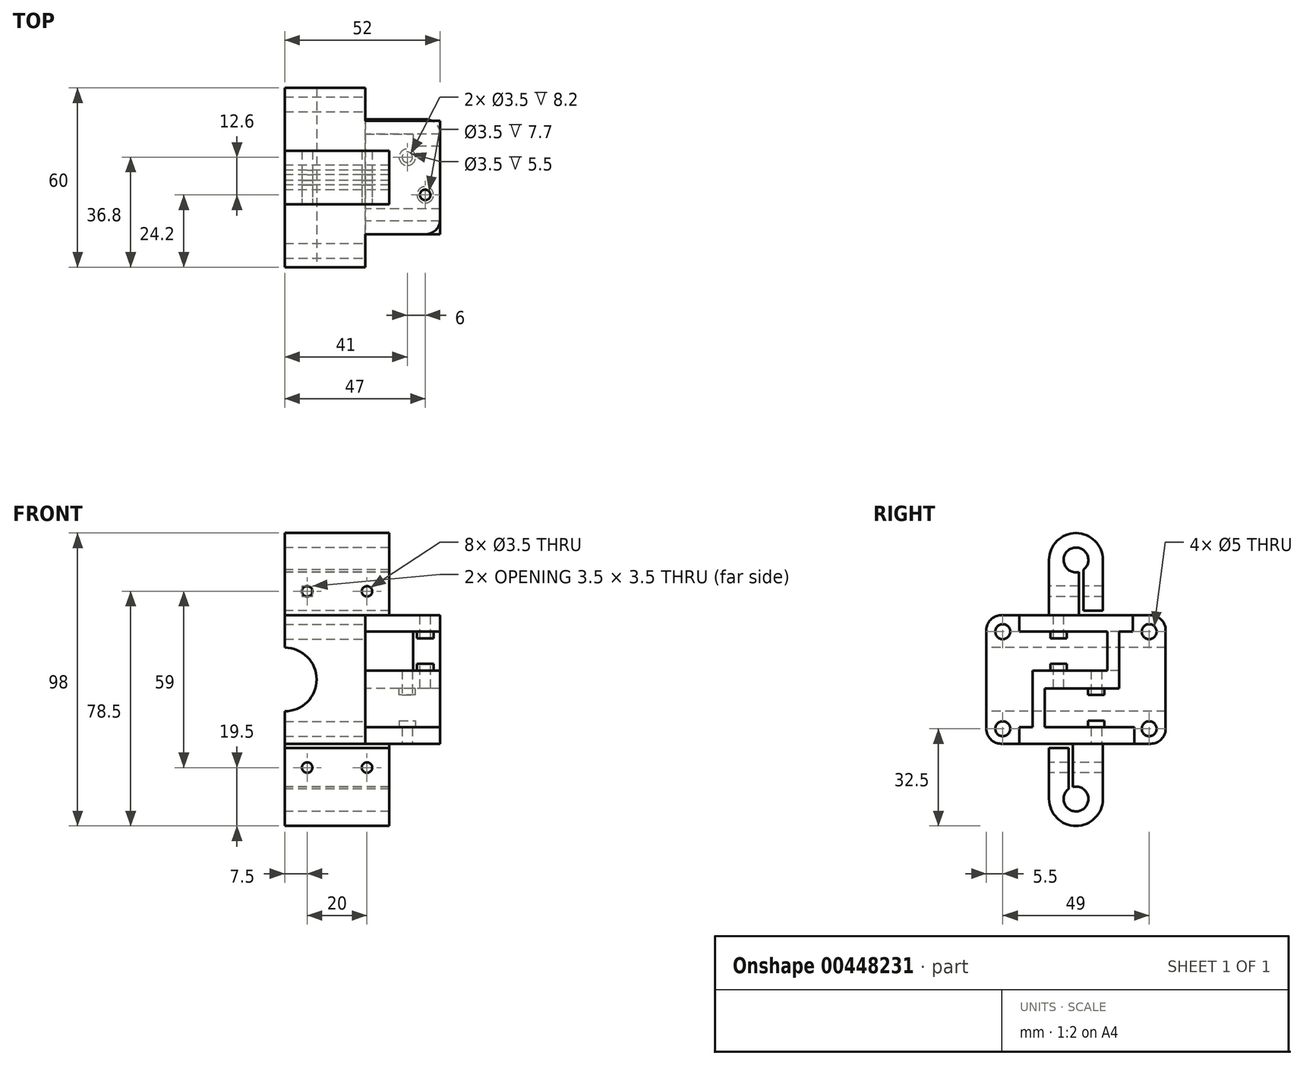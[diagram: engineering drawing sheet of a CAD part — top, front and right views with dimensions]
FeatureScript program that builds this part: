
annotation { "Feature Type Name" : "Feature", "Feature Type Description" : "" }
export const myFeature = defineFeature(function(context is Context, id is Id, definition is map)
    precondition{}
    {
        {
            var Q0;
            Q0=qCreatedBy(makeId("Front.planeOp"),FACE);
            var sketch = newSketch(context, id + "F0", { "sketchPlane" : qUnion([Q0])});
            skLineSegment(sketch, "E0.bottom", {"start": v(27, 21.5) * mm, "end": v(0, 21.5) * mm});
            skLineSegment(sketch, "E0.top", {"start": v(27, -21.5) * mm, "end": v(0, -21.5) * mm});
            skLineSegment(sketch, "E0.left", {"start": v(27, 21.5) * mm, "end": v(27, -21.5) * mm});
            skLineSegment(sketch, "E0.right", {"start": v(0, 21.5) * mm, "end": v(0, -21.5) * mm});
            skPoint(sketch, "E0.middle", {"position": v(0, 0) * mm});
            skSolve(sketch);
        }
        {
            var Q0;
            Q0=makeQuery(id+"F0.imprint","IMPRINT",FACE,{"disambiguationData":[TD([[makeQuery(id+"F0.imprint","IMPRINT",EDGE,{"derivedFrom":sQuery(id+"F0.wireOp",EDGE,"E0.bottom")}),1.0]])]});
            extrude(context, id + "F1", {"entities" : qUnion([Q0]), "endBound" : BoundingType.SYMMETRIC, "depth" : 60 * mm});
        }
        {
            var Q0;
            Q0=makeQuery(id+"F1.opExtrude","CAP_FACE",FACE,{"disambiguationData":[OSD([sQuery(id+"F0.wireOp",EDGE,"E0.bottom"),sQuery(id+"F0.wireOp",EDGE,"E0.top"),sQuery(id+"F0.wireOp",EDGE,"E0.left"),sQuery(id+"F0.wireOp",EDGE,"E0.right")])],"isStart":false});
            var sketch = newSketch(context, id + "F2", { "sketchPlane" : qUnion([Q0])});
            skCircle(sketch, "E1", {"center": v(0, 0) * mm, "radius": 10.65 * mm});
            skSolve(sketch);
        }
        {
            var Q0;
            {var subQ0=sQuery(id+"F2.wireOp",EDGE,"E1");var subQ1=makeQuery(id+"F1.opExtrude","CAP_EDGE",EDGE,{"disambiguationData":[OSD([sQuery(id+"F0.wireOp",EDGE,"E0.right")])],"isStart":false});var subQ2=makeQuery(id+"F2.imprint","INTERSECT",VERTEX,{"disambiguationData":[OD(0.0)],"derivedFrom":[subQ1,subQ0]});Q0=makeQuery(id+"F2.imprint","IMPRINT",FACE,{"disambiguationData":[TD([[makeQuery(id+"F2.imprint","IMPRINT",EDGE,{"disambiguationData":[TD([[subQ2,1.0]])],"derivedFrom":subQ0}),1.0]])]});}
            var Q1;
            {var subQ0=sQuery(id+"F2.wireOp",EDGE,"E1");var subQ1=makeQuery(id+"F1.opExtrude","CAP_EDGE",EDGE,{"disambiguationData":[OSD([sQuery(id+"F0.wireOp",EDGE,"E0.right")])],"isStart":false});var subQ2=makeQuery(id+"F2.imprint","INTERSECT",VERTEX,{"disambiguationData":[OD(0.0)],"derivedFrom":[subQ1,subQ0]});Q1=makeQuery(id+"F2.imprint","IMPRINT",FACE,{"disambiguationData":[TD([[makeQuery(id+"F2.imprint","IMPRINT",EDGE,{"disambiguationData":[TD([[subQ2,-1.0]])],"derivedFrom":subQ0}),1.0]])]});}
            var Q2;
            Q2=makeQuery(id+"F1.opExtrude","CAP_FACE",FACE,{"disambiguationData":[OSD([sQuery(id+"F0.wireOp",EDGE,"E0.bottom"),sQuery(id+"F0.wireOp",EDGE,"E0.top"),sQuery(id+"F0.wireOp",EDGE,"E0.left"),sQuery(id+"F0.wireOp",EDGE,"E0.right")])],"isStart":true});
            extrude(context, id + "F3", {"entities" : qUnion([Q0, Q1]), "operationType" : NewBodyOperationType.REMOVE, "endBound" : BoundingType.THROUGH_ALL, "oppositeDirection" : true, "endBoundEntityFace" : qUnion([Q2]), "depth" : 67.7 * mm});
        }
        {
            var Q0;
            Q0=makeQuery(id+"F1.opExtrude","SWEPT_FACE",FACE,{"disambiguationData":[OSD([sQuery(id+"F0.wireOp",EDGE,"E0.left")])]});
            var sketch = newSketch(context, id + "F4", { "sketchPlane" : qUnion([Q0])});
            skPoint(sketch, "E2", {"position": v(-24.5, 16) * mm});
            skPoint(sketch, "E3.1.0.0", {"position": v(24.5, 16) * mm});
            skLineSegment(sketch, "E3.direction1", {"start": v(-24.5, 16) * mm, "end": v(24.5, 16) * mm, "construction": true});
            skPoint(sketch, "E4.1.0.0", {"position": v(-24.5, -16.5) * mm});
            skPoint(sketch, "E4.1.0.1", {"position": v(24.5, -16.5) * mm});
            skLineSegment(sketch, "E4.direction1", {"start": v(-24.5, 16) * mm, "end": v(-24.5, -16.5) * mm, "construction": true});
            skSolve(sketch);
        }
        {
            var Q0;
            Q0=sQuery(id+"F4.wireOp",VERTEX,"E2");
            var Q1;
            Q1=sQuery(id+"F4.wireOp",VERTEX,"E3.1.0.0");
            var Q2;
            Q2=sQuery(id+"F4.wireOp",VERTEX,"E4.1.0.1");
            var Q3;
            Q3=sQuery(id+"F4.wireOp",VERTEX,"E4.1.0.0");
            var Q4;
            Q4=makeQuery(id+"F1.opExtrude","SWEPT_BODY",BODY,{"disambiguationData":[OSD([sQuery(id+"F0.wireOp",EDGE,"E0.bottom"),sQuery(id+"F0.wireOp",EDGE,"E0.top"),sQuery(id+"F0.wireOp",EDGE,"E0.left"),sQuery(id+"F0.wireOp",EDGE,"E0.right")])]});
            hole(context, id + "F5", {"style" : HoleStyle.SIMPLE, "endStyle" : HoleEndStyle.THROUGH, "holeDiameter" : 5 * mm, "isTappedThrough" : true, "tappedDepth" : 12 * mm, "tapClearance" : 3, "locations" : qUnion([Q0, Q1, Q2, Q3]), "scope" : qUnion([Q4])});
        }
        {
            var Q0;
            {var subQ0=sQuery(id+"F0.wireOp",EDGE,"E0.right");var subQ2=sQuery(id+"F0.wireOp",EDGE,"E0.top");Q0=makeQuery(id+"F3.boolean.opBoolean","SPLIT",FACE,{"disambiguationData":[TD([makeQuery(id+"F1.opExtrude","SWEPT_FACE",FACE,{"disambiguationData":[OSD([subQ2])]})])],"derivedFrom":makeQuery(id+"F1.opExtrude","SWEPT_FACE",FACE,{"disambiguationData":[OSD([subQ0])]})});}
            var sketch = newSketch(context, id + "F6", { "sketchPlane" : qUnion([Q0])});
            skLineSegment(sketch, "E5.bottom", {"start": v(9, 21.5) * mm, "end": v(-9, 21.5) * mm});
            skLineSegment(sketch, "E5.top", {"start": v(9, 40) * mm, "end": v(-9, 40) * mm});
            skLineSegment(sketch, "E5.left", {"start": v(9, 21.5) * mm, "end": v(9, 40) * mm});
            skLineSegment(sketch, "E5.right", {"start": v(-9, 21.5) * mm, "end": v(-9, 40) * mm});
            skLineSegment(sketch, "E6.bottom", {"start": v(9, -21.5) * mm, "end": v(-9, -21.5) * mm});
            skLineSegment(sketch, "E6.top", {"start": v(9, -40) * mm, "end": v(-9, -40) * mm});
            skLineSegment(sketch, "E6.left", {"start": v(9, -21.5) * mm, "end": v(9, -40) * mm});
            skLineSegment(sketch, "E6.right", {"start": v(-9, -21.5) * mm, "end": v(-9, -40) * mm});
            skArc(sketch, "E7", {"start": v(9, 40) * mm, "mid": v(0, 49) * mm, "end": v(-9, 40) * mm});
            skArc(sketch, "E8", {"start": v(-9, -40) * mm, "mid": v(0, -49) * mm, "end": v(9, -40) * mm});
            skLineSegment(sketch, "E9", {"start": v(0, 21.5) * mm, "end": v(0, -21.5) * mm, "construction": true});
            skPoint(sketch, "E9.startSnap0", {"position": v(0, 21.5) * mm});
            skSolve(sketch);
        }
        {
            var Q0;
            Q0=makeQuery(id+"F6.imprint","IMPRINT",FACE,{"disambiguationData":[TD([[makeQuery(id+"F6.imprint","IMPRINT",EDGE,{"derivedFrom":sQuery(id+"F6.wireOp",EDGE,"E5.bottom")}),-1.0]])]});
            var Q1;
            Q1=makeQuery(id+"F6.imprint","IMPRINT",FACE,{"disambiguationData":[TD([[makeQuery(id+"F6.imprint","IMPRINT",EDGE,{"derivedFrom":sQuery(id+"F6.wireOp",EDGE,"E5.top")}),-1.0]])]});
            var Q2;
            Q2=makeQuery(id+"F6.imprint","IMPRINT",FACE,{"disambiguationData":[TD([[makeQuery(id+"F6.imprint","IMPRINT",EDGE,{"derivedFrom":sQuery(id+"F6.wireOp",EDGE,"E6.bottom")}),1.0]])]});
            var Q3;
            Q3=makeQuery(id+"F6.imprint","IMPRINT",FACE,{"disambiguationData":[TD([[makeQuery(id+"F6.imprint","IMPRINT",EDGE,{"derivedFrom":sQuery(id+"F6.wireOp",EDGE,"E6.top")}),1.0]])]});
            extrude(context, id + "F7", {"entities" : qUnion([Q0, Q1, Q2, Q3]), "operationType" : NewBodyOperationType.ADD, "oppositeDirection" : true, "depth" : 35 * mm});
        }
        {
            var Q0;
            Q0=sQuery(id+"F6.wireOp",VERTEX,"E8.center");
            var Q1;
            Q1=sQuery(id+"F6.wireOp",VERTEX,"E7.center");
            var Q2;
            Q2=makeQuery(id+"F1.opExtrude","SWEPT_BODY",BODY,{"disambiguationData":[OSD([sQuery(id+"F0.wireOp",EDGE,"E0.bottom"),sQuery(id+"F0.wireOp",EDGE,"E0.top"),sQuery(id+"F0.wireOp",EDGE,"E0.left"),sQuery(id+"F0.wireOp",EDGE,"E0.right")])]});
            hole(context, id + "F8", {"style" : HoleStyle.SIMPLE, "endStyle" : HoleEndStyle.THROUGH, "holeDiameter" : 8.3 * mm, "isTappedThrough" : true, "tappedDepth" : 12 * mm, "tapClearance" : 3, "locations" : qUnion([Q0, Q1]), "scope" : qUnion([Q2])});
        }
        {
            var Q0;
            Q0=makeQuery(id+"F1.opExtrude","SWEPT_FACE",FACE,{"disambiguationData":[OSD([sQuery(id+"F0.wireOp",EDGE,"E0.left")])]});
            var sketch = newSketch(context, id + "F9", { "sketchPlane" : qUnion([Q0])});
            skLineSegment(sketch, "E10", {"start": v(-19, 21.5) * mm, "end": v(-19, 16) * mm});
            skLineSegment(sketch, "E11", {"start": v(-19, 16) * mm, "end": v(10.5, 16) * mm});
            skLineSegment(sketch, "E12", {"start": v(10.5, 16) * mm, "end": v(10.5, 3) * mm});
            skLineSegment(sketch, "E13", {"start": v(-10.5, -3) * mm, "end": v(14.5, -3) * mm});
            skLineSegment(sketch, "E14", {"start": v(14.5, -3) * mm, "end": v(14.5, 16) * mm});
            skLineSegment(sketch, "E15", {"start": v(14.5, 16) * mm, "end": v(19, 16) * mm});
            skLineSegment(sketch, "E16", {"start": v(19, 16) * mm, "end": v(19, 21.5) * mm});
            skLineSegment(sketch, "E17", {"start": v(19, 21.5) * mm, "end": v(-19, 21.5) * mm});
            skLineSegment(sketch, "E18", {"start": v(10.5, 3) * mm, "end": v(-14.5, 3) * mm});
            skLineSegment(sketch, "E19", {"start": v(-12, -21.5) * mm, "end": v(19.5, -21.5) * mm});
            skLineSegment(sketch, "E20", {"start": v(19.5, -21.5) * mm, "end": v(19.5, -16) * mm});
            skLineSegment(sketch, "E21", {"start": v(19.5, -16) * mm, "end": v(-14.68, -16) * mm});
            skLineSegment(sketch, "E22", {"start": v(-8.55, -16) * mm, "end": v(-19, -16) * mm});
            skLineSegment(sketch, "E23", {"start": v(-19, -16) * mm, "end": v(-19, -21.5) * mm});
            skLineSegment(sketch, "E24", {"start": v(-19, -21.5) * mm, "end": v(19.5, -21.5) * mm});
            skLineSegment(sketch, "E25", {"start": v(-10.5, -16) * mm, "end": v(-10.5, -3) * mm});
            skLineSegment(sketch, "E26", {"start": v(-14.5, 3) * mm, "end": v(-14.5, -16) * mm});
            skSolve(sketch);
        }
        {
            var Q0;
            {var subQ12=sQuery(id+"F9.wireOp",EDGE,"E10");Q0=makeQuery(id+"F9.imprint","IMPRINT",FACE,{"disambiguationData":[TD([[makeQuery(id+"F9.imprint","IMPRINT",EDGE,{"derivedFrom":subQ12}),1.0]])]});}
            var Q1;
            {var subQ5=sQuery(id+"F9.wireOp",EDGE,"E20");Q1=makeQuery(id+"F9.imprint","IMPRINT",FACE,{"disambiguationData":[TD([[makeQuery(id+"F9.imprint","IMPRINT",EDGE,{"derivedFrom":subQ5}),1.0]])]});}
            extrude(context, id + "F10", {"entities" : qUnion([Q0, Q1]), "operationType" : NewBodyOperationType.ADD, "depth" : 25 * mm});
        }
        {
            var Q0;
            Q0=makeQuery(id+"F10.opExtrude","SWEPT_FACE",FACE,{"disambiguationData":[OSD([sQuery(id+"F9.wireOp",EDGE,"E12")])]});
            var sketch = newSketch(context, id + "F11", { "sketchPlane" : qUnion([Q0])});
            skLineSegment(sketch, "E27.bottom", {"start": v(27, 16) * mm, "end": v(43, 16) * mm});
            skLineSegment(sketch, "E27.top", {"start": v(27, 3) * mm, "end": v(43, 3) * mm});
            skLineSegment(sketch, "E27.left", {"start": v(27, 16) * mm, "end": v(27, 3) * mm});
            skLineSegment(sketch, "E27.right", {"start": v(43, 16) * mm, "end": v(43, 3) * mm});
            skSolve(sketch);
        }
        {
            var Q0;
            Q0=makeQuery(id+"F11.imprint","IMPRINT",FACE,{"disambiguationData":[TD([[makeQuery(id+"F11.imprint","IMPRINT",EDGE,{"derivedFrom":sQuery(id+"F11.wireOp",EDGE,"E27.bottom")}),1.0]])]});
            extrude(context, id + "F12", {"entities" : qUnion([Q0]), "operationType" : NewBodyOperationType.REMOVE, "endBound" : BoundingType.UP_TO_NEXT, "oppositeDirection" : true, "depth" : 25 * mm});
        }
        {
            var Q0;
            {var subQ6=sQuery(id+"F6.wireOp",EDGE,"E5.right");var subQ7=sQuery(id+"F6.wireOp",EDGE,"E5.left");var subQ10=sQuery(id+"F0.wireOp",EDGE,"E0.bottom");var subQ11=makeQuery(id+"F1.opExtrude","SWEPT_FACE",FACE,{"disambiguationData":[OSD([subQ10])]});Q0=makeQuery(id+"F10.boolean.opBoolean","MERGE",FACE,{"derivedFrom":[makeQuery(id+"F7.boolean.opBoolean","SPLIT",FACE,{"disambiguationData":[TD([makeQuery(id+"F7.opExtrude","SWEPT_FACE",FACE,{"disambiguationData":[OSD([subQ6])]})])],"derivedFrom":subQ11}),makeQuery(id+"F7.boolean.opBoolean","SPLIT",FACE,{"disambiguationData":[TD([makeQuery(id+"F7.opExtrude","SWEPT_FACE",FACE,{"disambiguationData":[OSD([subQ7])]})])],"derivedFrom":subQ11}),makeQuery(id+"F10.opExtrude","SWEPT_FACE",FACE,{"disambiguationData":[OSD([sQuery(id+"F9.wireOp",EDGE,"E17")])]})]});}
            var sketch = newSketch(context, id + "F13", { "sketchPlane" : qUnion([Q0])});
            skPoint(sketch, "E28", {"position": v(47, -5.8) * mm});
            skSolve(sketch);
        }
        {
            var Q0;
            Q0=sQuery(id+"F13.wireOp",VERTEX,"E28");
            var Q1;
            Q1=makeQuery(id+"F1.opExtrude","SWEPT_BODY",BODY,{"disambiguationData":[OSD([sQuery(id+"F0.wireOp",EDGE,"E0.bottom"),sQuery(id+"F0.wireOp",EDGE,"E0.top"),sQuery(id+"F0.wireOp",EDGE,"E0.left"),sQuery(id+"F0.wireOp",EDGE,"E0.right")])]});
            hole(context, id + "F14", {"style" : HoleStyle.SIMPLE, "endStyle" : HoleEndStyle.BLIND, "holeDiameter" : 3.5 * mm, "holeDepth" : 26 * mm, "isTappedThrough" : true, "tappedDepth" : 12 * mm, "tapClearance" : 3, "locations" : qUnion([Q0]), "scope" : qUnion([Q1])});
        }
        {
            var Q0;
            {var subQ6=sQuery(id+"F0.wireOp",EDGE,"E0.top");var subQ8=sQuery(id+"F6.wireOp",EDGE,"E6.right");var subQ9=sQuery(id+"F6.wireOp",EDGE,"E6.left");var subQ11=makeQuery(id+"F1.opExtrude","SWEPT_FACE",FACE,{"disambiguationData":[OSD([subQ6])]});Q0=makeQuery(id+"F10.boolean.opBoolean","MERGE",FACE,{"derivedFrom":[makeQuery(id+"F7.boolean.opBoolean","SPLIT",FACE,{"disambiguationData":[TD([makeQuery(id+"F7.opExtrude","SWEPT_FACE",FACE,{"disambiguationData":[OSD([subQ8])]})])],"derivedFrom":subQ11}),makeQuery(id+"F7.boolean.opBoolean","SPLIT",FACE,{"disambiguationData":[TD([makeQuery(id+"F7.opExtrude","SWEPT_FACE",FACE,{"disambiguationData":[OSD([subQ9])]})])],"derivedFrom":subQ11}),makeQuery(id+"F10.opExtrude","SWEPT_FACE",FACE,{"disambiguationData":[OSD([sQuery(id+"F9.wireOp",EDGE,"E24")])]})]});}
            var sketch = newSketch(context, id + "F15", { "sketchPlane" : qUnion([Q0])});
            skPoint(sketch, "E29", {"position": v(41, -6.8) * mm});
            skSolve(sketch);
        }
        {
            var Q0;
            Q0=sQuery(id+"F15.wireOp",VERTEX,"E29");
            var Q1;
            Q1=makeQuery(id+"F1.opExtrude","SWEPT_BODY",BODY,{"disambiguationData":[OSD([sQuery(id+"F0.wireOp",EDGE,"E0.bottom"),sQuery(id+"F0.wireOp",EDGE,"E0.top"),sQuery(id+"F0.wireOp",EDGE,"E0.left"),sQuery(id+"F0.wireOp",EDGE,"E0.right")])]});
            hole(context, id + "F16", {"style" : HoleStyle.SIMPLE, "endStyle" : HoleEndStyle.BLIND, "holeDiameter" : 3.5 * mm, "holeDepth" : 26 * mm, "isTappedThrough" : true, "tappedDepth" : 12 * mm, "tapClearance" : 3, "locations" : qUnion([Q0]), "scope" : qUnion([Q1])});
        }
        {
            var Q0;
            Q0=makeQuery(id+"F10.opExtrude","SWEPT_FACE",FACE,{"disambiguationData":[OSD([sQuery(id+"F9.wireOp",EDGE,"E13")])]});
            var sketch = newSketch(context, id + "F17", { "sketchPlane" : qUnion([Q0])});
            skCircle(sketch, "E30.0", {"center": v(41, -6.8) * mm, "radius": 2.75 * mm});
            skSolve(sketch);
        }
        {
            var Q0;
            Q0=makeQuery(id+"F17.imprint","IMPRINT",FACE,{"disambiguationData":[TD([[makeQuery(id+"F17.imprint","IMPRINT",EDGE,{"derivedFrom":sQuery(id+"F17.wireOp",EDGE,"E30.0")}),1.0]])]});
            extrude(context, id + "F18", {"entities" : qUnion([Q0]), "operationType" : NewBodyOperationType.ADD, "depth" : 2.2 * mm});
        }
        {
            var Q0;
            Q0=makeQuery(id+"F10.opExtrude","SWEPT_FACE",FACE,{"disambiguationData":[OSD([sQuery(id+"F9.wireOp",EDGE,"E21"),sQuery(id+"F9.wireOp",EDGE,"E22")])]});
            var sketch = newSketch(context, id + "F19", { "sketchPlane" : qUnion([Q0])});
            skCircle(sketch, "E31.0", {"center": v(41, 6.8) * mm, "radius": 2.75 * mm});
            skSolve(sketch);
        }
        {
            var Q0;
            Q0=makeQuery(id+"F19.imprint","IMPRINT",FACE,{"disambiguationData":[TD([[makeQuery(id+"F19.imprint","IMPRINT",EDGE,{"derivedFrom":sQuery(id+"F19.wireOp",EDGE,"E31.0")}),1.0]])]});
            extrude(context, id + "F20", {"entities" : qUnion([Q0]), "operationType" : NewBodyOperationType.ADD, "depth" : 2.2 * mm});
        }
        {
            var Q0;
            Q0=makeQuery(id+"F12.boolean.opBoolean","MERGE",FACE,{"derivedFrom":[makeQuery(id+"F10.opExtrude","SWEPT_FACE",FACE,{"disambiguationData":[OSD([sQuery(id+"F9.wireOp",EDGE,"E11")])]}),makeQuery(id+"F10.opExtrude","SWEPT_FACE",FACE,{"disambiguationData":[OSD([sQuery(id+"F9.wireOp",EDGE,"E15")])]}),makeQuery(id+"F12.opExtrude","SWEPT_FACE",FACE,{"disambiguationData":[OSD([sQuery(id+"F11.wireOp",EDGE,"E27.bottom")])]})]});
            var sketch = newSketch(context, id + "F21", { "sketchPlane" : qUnion([Q0])});
            skCircle(sketch, "E32.0", {"center": v(47, 5.8) * mm, "radius": 2.75 * mm});
            skSolve(sketch);
        }
        {
            var Q0;
            Q0=makeQuery(id+"F21.imprint","IMPRINT",FACE,{"disambiguationData":[TD([[makeQuery(id+"F21.imprint","IMPRINT",EDGE,{"derivedFrom":sQuery(id+"F21.wireOp",EDGE,"E32.0")}),1.0]])]});
            extrude(context, id + "F22", {"entities" : qUnion([Q0]), "operationType" : NewBodyOperationType.ADD, "depth" : 2.2 * mm});
        }
        {
            var Q0;
            Q0=makeQuery(id+"F12.boolean.opBoolean","MERGE",FACE,{"derivedFrom":[makeQuery(id+"F10.opExtrude","SWEPT_FACE",FACE,{"disambiguationData":[OSD([sQuery(id+"F9.wireOp",EDGE,"E18")])]}),makeQuery(id+"F12.opExtrude","SWEPT_FACE",FACE,{"disambiguationData":[OSD([sQuery(id+"F11.wireOp",EDGE,"E27.top")])]})]});
            var sketch = newSketch(context, id + "F23", { "sketchPlane" : qUnion([Q0])});
            skCircle(sketch, "E33.0", {"center": v(47, -5.8) * mm, "radius": 2.75 * mm});
            skSolve(sketch);
        }
        {
            var Q0;
            Q0=makeQuery(id+"F23.imprint","IMPRINT",FACE,{"disambiguationData":[TD([[makeQuery(id+"F23.imprint","IMPRINT",EDGE,{"derivedFrom":sQuery(id+"F23.wireOp",EDGE,"E33.0")}),1.0]])]});
            extrude(context, id + "F24", {"entities" : qUnion([Q0]), "operationType" : NewBodyOperationType.ADD, "depth" : 2.2 * mm});
        }
        {
            var Q0;
            {var subQ0=sQuery(id+"F0.wireOp",EDGE,"E0.bottom");var subQ1=sQuery(id+"F0.wireOp",EDGE,"E0.right");Q0=makeQuery(id+"F7.boolean.opBoolean","MERGE",FACE,{"derivedFrom":[makeQuery(id+"F3.boolean.opBoolean","SPLIT",FACE,{"disambiguationData":[TD([makeQuery(id+"F1.opExtrude","SWEPT_FACE",FACE,{"disambiguationData":[OSD([subQ0])]})])],"derivedFrom":makeQuery(id+"F1.opExtrude","SWEPT_FACE",FACE,{"disambiguationData":[OSD([subQ1])]})}),makeQuery(id+"F7.opExtrude","CAP_FACE",FACE,{"disambiguationData":[OSD([sQuery(id+"F6.wireOp",EDGE,"E5.bottom"),sQuery(id+"F6.wireOp",EDGE,"E5.left"),sQuery(id+"F6.wireOp",EDGE,"E5.right"),sQuery(id+"F6.wireOp",EDGE,"E7")])],"isStart":true})]});}
            var sketch = newSketch(context, id + "F25", { "sketchPlane" : qUnion([Q0])});
            skLineSegment(sketch, "E34", {"start": v(-1, 39.5) * mm, "end": v(-1, 21.5) * mm});
            skLineSegment(sketch, "E35", {"start": v(-1, 21.5) * mm, "end": v(-11, 21.5) * mm});
            skLineSegment(sketch, "E36", {"start": v(1, -39.5) * mm, "end": v(1, -21.5) * mm});
            skLineSegment(sketch, "E37", {"start": v(1, -21.5) * mm, "end": v(11, -21.5) * mm});
            skLineSegment(sketch, "E38.0", {"start": v(2.5, -23) * mm, "end": v(11, -23) * mm});
            skLineSegment(sketch, "E38.1", {"start": v(2.5, -39.5) * mm, "end": v(2.5, -23) * mm});
            skLineSegment(sketch, "E39.0", {"start": v(-2.5, 23) * mm, "end": v(-11, 23) * mm});
            skLineSegment(sketch, "E39.1", {"start": v(-2.5, 39.5) * mm, "end": v(-2.5, 23) * mm});
            skLineSegment(sketch, "E40", {"start": v(11, -21.5) * mm, "end": v(11, -23) * mm});
            skLineSegment(sketch, "E41", {"start": v(1, -39.5) * mm, "end": v(2.5, -39.5) * mm});
            skLineSegment(sketch, "E42", {"start": v(-2.5, 39.5) * mm, "end": v(-1, 39.5) * mm});
            skLineSegment(sketch, "E43", {"start": v(-11, 21.5) * mm, "end": v(-11, 23) * mm});
            skSolve(sketch);
        }
        {
            var Q0;
            {var subQ3=makeQuery(id+"F7.opExtrude","CAP_EDGE",EDGE,{"disambiguationData":[OSD([sQuery(id+"F6.wireOp",EDGE,"E5.right")])],"isStart":true});var subQ5=sQuery(id+"F25.wireOp",EDGE,"E35");var subQ6=makeQuery(id+"F25.imprint","INTERSECT",VERTEX,{"derivedFrom":[subQ3,subQ5]});Q0=makeQuery(id+"F25.imprint","IMPRINT",FACE,{"disambiguationData":[TD([[makeQuery(id+"F25.imprint","IMPRINT",EDGE,{"disambiguationData":[TD([[subQ6,1.0]])],"derivedFrom":subQ5}),-1.0]])]});}
            var Q1;
            Q1=makeQuery(id+"F25.imprint","IMPRINT",FACE,{"disambiguationData":[TD([[makeQuery(id+"F25.imprint","IMPRINT",EDGE,{"derivedFrom":sQuery(id+"F25.wireOp",EDGE,"E36")}),-1.0]])]});
            extrude(context, id + "F26", {"entities" : qUnion([Q0, Q1]), "operationType" : NewBodyOperationType.REMOVE, "endBound" : BoundingType.THROUGH_ALL, "oppositeDirection" : true, "depth" : 25 * mm});
        }
        {
            var Q0;
            Q0=makeQuery(id+"F1.opExtrude","CAP_EDGE",EDGE,{"disambiguationData":[OSD([sQuery(id+"F0.wireOp",EDGE,"E0.bottom")])],"isStart":false});
            var Q1;
            Q1=makeQuery(id+"F1.opExtrude","CAP_EDGE",EDGE,{"disambiguationData":[OSD([sQuery(id+"F0.wireOp",EDGE,"E0.top")])],"isStart":false});
            var Q2;
            Q2=makeQuery(id+"F1.opExtrude","CAP_EDGE",EDGE,{"disambiguationData":[OSD([sQuery(id+"F0.wireOp",EDGE,"E0.top")])],"isStart":true});
            var Q3;
            Q3=makeQuery(id+"F1.opExtrude","CAP_EDGE",EDGE,{"disambiguationData":[OSD([sQuery(id+"F0.wireOp",EDGE,"E0.bottom")])],"isStart":true});
            var Q4;
            Q4=makeQuery(id+"F10.opExtrude","CAP_EDGE",EDGE,{"disambiguationData":[OSD([sQuery(id+"F9.wireOp",EDGE,"E10")])],"isStart":false});
            var Q5;
            Q5=makeQuery(id+"F10.opExtrude","CAP_EDGE",EDGE,{"disambiguationData":[OSD([sQuery(id+"F9.wireOp",EDGE,"E20")])],"isStart":false});
            fillet(context, id + "F27", {"entities" : qUnion([Q0, Q1, Q2, Q3, Q4, Q5]), "radius" : 5 * mm, "tangentPropagation" : true, "allowEdgeOverflow" : false});
        }
        {
            var Q0;
            Q0=makeQuery(id+"F7.opExtrude","SWEPT_FACE",FACE,{"disambiguationData":[OSD([sQuery(id+"F6.wireOp",EDGE,"E6.left")])]});
            var sketch = newSketch(context, id + "F28", { "sketchPlane" : qUnion([Q0])});
            skPoint(sketch, "E44", {"position": v(7.5, -29.5) * mm});
            skLineSegment(sketch, "E45", {"start": v(17.5, -40) * mm, "end": v(17.5, -23) * mm, "construction": true});
            skPoint(sketch, "E46.MirrorP", {"position": v(27.5, -29.5) * mm});
            skPoint(sketch, "E47.MirrorP", {"position": v(7.5, 29.5) * mm});
            skPoint(sketch, "E48.MirrorP", {"position": v(27.5, 29.5) * mm});
            skSolve(sketch);
        }
        {
            var Q0;
            Q0=sQuery(id+"F28.wireOp",VERTEX,"E44");
            var Q1;
            Q1=sQuery(id+"F28.wireOp",VERTEX,"E46.MirrorP");
            var Q2;
            Q2=sQuery(id+"F28.wireOp",VERTEX,"E47.MirrorP");
            var Q3;
            Q3=sQuery(id+"F28.wireOp",VERTEX,"E48.MirrorP");
            var Q4;
            Q4=makeQuery(id+"F1.opExtrude","SWEPT_BODY",BODY,{"disambiguationData":[OSD([sQuery(id+"F0.wireOp",EDGE,"E0.bottom"),sQuery(id+"F0.wireOp",EDGE,"E0.top"),sQuery(id+"F0.wireOp",EDGE,"E0.left"),sQuery(id+"F0.wireOp",EDGE,"E0.right")])]});
            hole(context, id + "F29", {"style" : HoleStyle.SIMPLE, "endStyle" : HoleEndStyle.THROUGH, "holeDiameter" : 3.5 * mm, "isTappedThrough" : true, "tappedDepth" : 12 * mm, "tapClearance" : 3, "locations" : qUnion([Q0, Q1, Q2, Q3]), "scope" : qUnion([Q4])});
        }
    });
